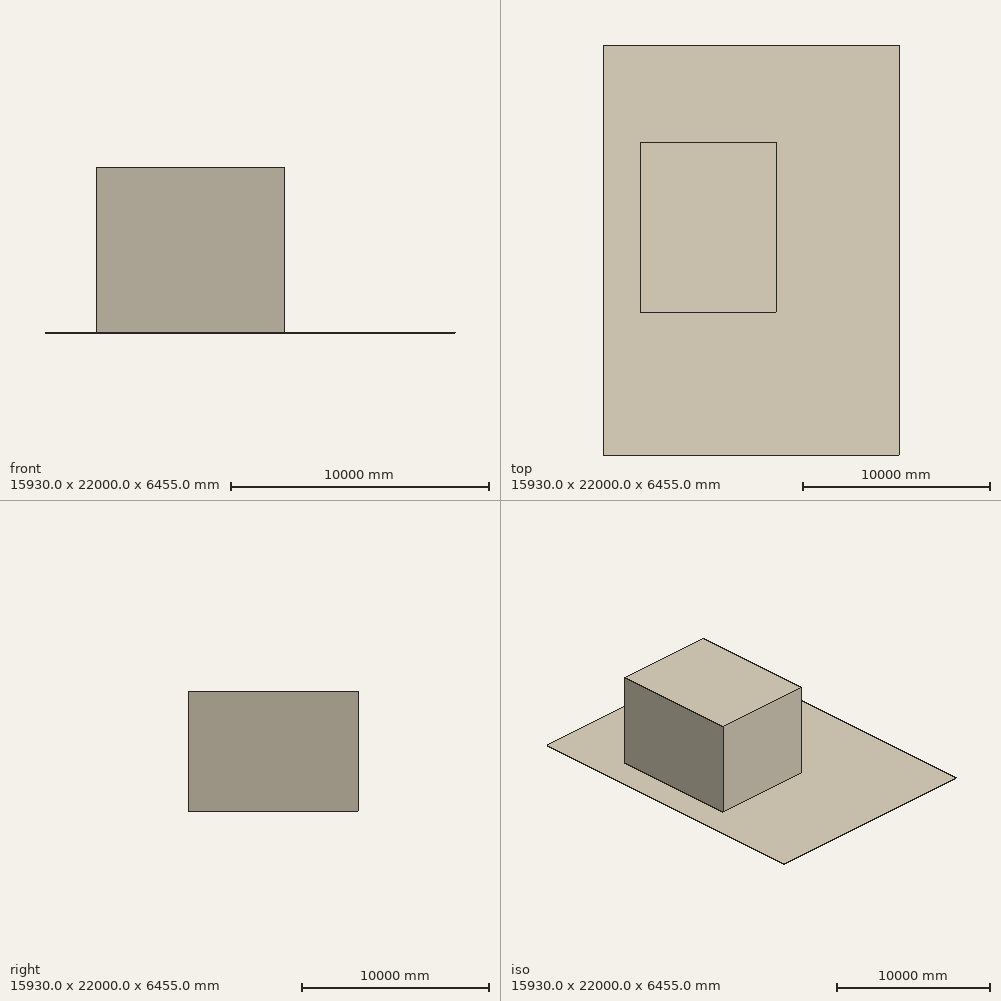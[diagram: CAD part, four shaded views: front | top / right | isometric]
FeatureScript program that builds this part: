
annotation { "Feature Type Name" : "Feature", "Feature Type Description" : "" }
export const myFeature = defineFeature(function(context is Context, id is Id, definition is map)
    precondition{}
    {
        {
            var Q0;
            Q0=qCreatedBy(makeId("Top.planeOp"),FACE);
            var sketch = newSketch(context, id + "F0", { "sketchPlane" : qUnion([Q0])});
            skLineSegment(sketch, "E0.bottom", {"start": v(-7959.9, 15431.85) * mm, "end": v(7970.1, 15431.85) * mm});
            skLineSegment(sketch, "E0.top", {"start": v(-7959.9, -6568.15) * mm, "end": v(7970.1, -6568.15) * mm});
            skLineSegment(sketch, "E0.left", {"start": v(-7959.9, 15431.85) * mm, "end": v(-7959.9, -6568.15) * mm});
            skLineSegment(sketch, "E0.right", {"start": v(7970.1, 15431.85) * mm, "end": v(7970.1, -6568.15) * mm});
            skSolve(sketch);
        }
        {
            var Q0;
            Q0 = qSketchRegion(id + "F0", true);
            var Q1;
            Q1=makeQuery(id+"F0.imprint","IMPRINT",FACE,{"disambiguationData":[TD([[makeQuery(id+"F0.imprint","IMPRINT",EDGE,{"derivedFrom":sQuery(id+"F0.wireOp",EDGE,"E0.bottom")}),-1.0]])]});
            extrude(context, id + "F1", {"entities" : qUnion([Q0, Q1]), "depth" : 25 * mm});
        }
        {
            var Q0;
            Q0=makeQuery(id+"F1.opExtrude","CAP_FACE",FACE,{"disambiguationData":[OSD([sQuery(id+"F0.wireOp",EDGE,"E0.bottom"),sQuery(id+"F0.wireOp",EDGE,"E0.top"),sQuery(id+"F0.wireOp",EDGE,"E0.left"),sQuery(id+"F0.wireOp",EDGE,"E0.right")])],"isStart":false});
            var sketch = newSketch(context, id + "F2", { "sketchPlane" : qUnion([Q0])});
            skLineSegment(sketch, "E1", {"start": v(-5959.9, 15431.85) * mm, "end": v(-5959.9, -4877.25) * mm, "construction": true});
            skLineSegment(sketch, "E2", {"start": v(-7959.9, 10201.85) * mm, "end": v(7970.1, 10201.85) * mm, "construction": true});
            skPoint(sketch, "E3", {"position": v(-5959.9, 10201.85) * mm});
            skLineSegment(sketch, "E4.bottom", {"start": v(-5959.9, 10201.85) * mm, "end": v(1320.1, 10201.85) * mm});
            skLineSegment(sketch, "E4.top", {"start": v(-5959.9, 1101.85) * mm, "end": v(1320.1, 1101.85) * mm});
            skLineSegment(sketch, "E4.left", {"start": v(-5959.9, 10201.85) * mm, "end": v(-5959.9, 1101.85) * mm});
            skLineSegment(sketch, "E4.right", {"start": v(1320.1, 10201.85) * mm, "end": v(1320.1, 1101.85) * mm});
            skSolve(sketch);
        }
        {
            var Q0;
            Q0 = qSketchRegion(id + "F2", true);
            var Q1;
            Q1=makeQuery(id+"F2.imprint","IMPRINT",FACE,{"disambiguationData":[TD([[makeQuery(id+"F2.imprint","IMPRINT",EDGE,{"derivedFrom":sQuery(id+"F2.wireOp",EDGE,"E4.bottom")}),-1.0]])]});
            extrude(context, id + "F3", {"entities" : qUnion([Q0, Q1]), "operationType" : NewBodyOperationType.ADD, "depth" : 6430 * mm});
        }
    });
